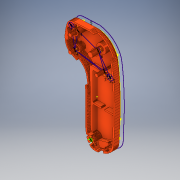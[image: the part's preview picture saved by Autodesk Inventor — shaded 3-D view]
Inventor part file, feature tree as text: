
AUTODESK INVENTOR PART (.ipt)
format: ipt  version: 2019.4 (Build 234330000, 330)  size: 12,663,808 bytes
history: native  units: mm
features: sketch x4, other x2, shell x1, surface_op x1, projected_geometry x1
ambient origin geometry x8: Origin, YZ Plane, XZ Plane, XY Plane, X Axis, Y Axis, Z Axis, Center Point
bodies: Solid1 (feature_tree)
feature tree (9):
  shell  "shell-bottom"  Thickness=5.0mm
  surface_op  "Sculpt1"
  sketch  "Sketch1"  dims[d1=2.5mm]
  sketch  "Sketch2"  dims[d2=7.0mm]
  sketch  "Sketch3"  dims[d3=4.0mm]
  sketch  "Sketch4"  dims[d4=6.0mm d5=4.0mm d6=2.5mm d7=4.0mm d8=2.5mm d9=7.0mm d10=3.5mm]
  projected_geometry  "Projected Loop1"
  other  "MeshFeature1"
  other  "Srf1"
